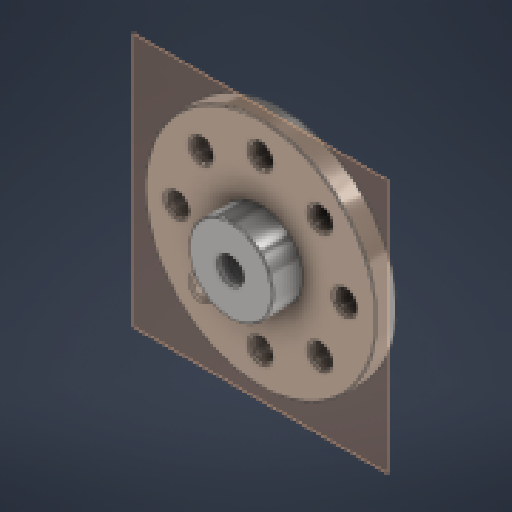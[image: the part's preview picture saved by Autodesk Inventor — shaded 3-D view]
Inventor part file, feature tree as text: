
AUTODESK INVENTOR PART (.ipt)
format: ipt  version: 2024 (Build 280153000, 153)  size: 205,312 bytes
history: native  units: mm
features: other x7, sketch x2, extrude x2, reference x2, fillet x1, chamfer x1, projected_geometry x1
ambient origin geometry x8: Origin, YZ Plane, XZ Plane, XY Plane, X Axis, Y Axis, Z Axis, Center Point
bodies: Body1 (feature_tree)
feature tree (16):
  other  "솔리드1"
  other  "작업 평면1"
  sketch  "스케치1"
  other  "작업 평면2"
  extrude  "돌출1"  Depth=2.5mm
  sketch  "스케치2"
  other  "작업 평면3"
  extrude  "돌출2"  Depth=10.0mm TaperAngle=0.0deg
  fillet  "모깎기1"  Radius=10.0mm
  other  "스레드1"
  chamfer  "모따기1"  Distance=0.1mm
  reference  "참조1"
  reference  "참조2"
  projected_geometry  "투영된 루프1"
  other  "MX-28T_R+idle.ipt.iam"
  other  "MX-28T_R:1"
